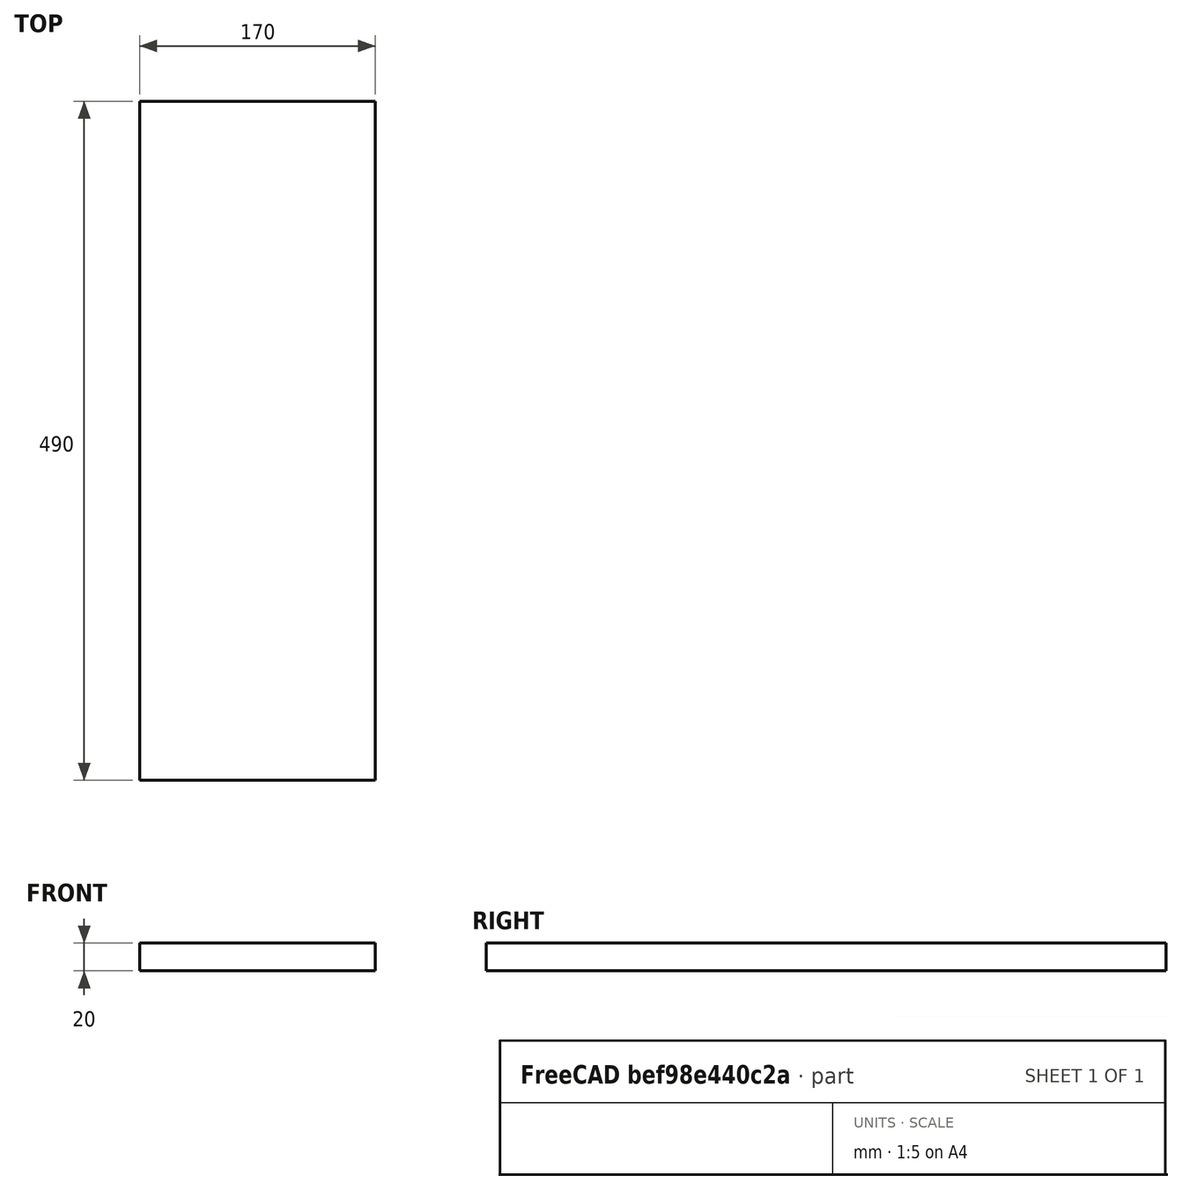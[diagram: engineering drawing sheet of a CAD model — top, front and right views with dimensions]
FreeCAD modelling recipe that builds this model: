
FCSTD DOCUMENT  (FreeCAD 0.18R16131 (Git))
Label: 700_ASM_Cabinet_Roof
License: All rights reserved
LicenseURL: http://en.wikipedia.org/wiki/All_rights_reserved
objects: Sketcher::SketchObject×1, PartDesign::Pad×1, PartDesign::Body×1, Spreadsheet::Sheet×1
note: 4 computed .brp shape members not serialized (recipe doc carries the construction recipe); baked Part::Feature solids carry a one-line shape summary decoded from their .brp

FEATURE [Sketcher::SketchObject] Sketch
  MapMode = 5
  Support = -> [XY_Plane]
  expr: Constraints[5] = xls.k_w
  sketch-geometry (5):
    g0: LineSegment StartX=0 StartY=490 StartZ=0 EndX=170 EndY=490 EndZ=0
    g1: LineSegment StartX=170 StartY=490 StartZ=0 EndX=170 EndY=0 EndZ=0
    g2: LineSegment StartX=170 StartY=0 StartZ=0 EndX=0 EndY=0 EndZ=0
    g3: LineSegment StartX=0 StartY=0 StartZ=0 EndX=0 EndY=245 EndZ=0
    g4: LineSegment StartX=0 StartY=245 StartZ=0 EndX=0 EndY=490 EndZ=0
  constraints (14):
    c: Coincident(g0,g1)
    c: Coincident(g1,g2)
    c: Horizontal(g0)
    c: Horizontal(g2)
    c: Vertical(g1)
    c: DistanceY(g1,g1) = 490
    c: DistanceX(g0,g0) = 170
    c: Coincident(g3,g2)
    c: Coincident(g4,g0)
    c: Equal(g3,g4)
    c: Vertical(g4)
    c: Vertical(g3)
    c: Coincident(g3,g4)
    c: Coincident(g2,g-1)
FEATURE [PartDesign::Pad] Pad
  Length = 20
  Length2 = 100
  Profile = -> Sketch
  Type = 0
  expr: Length = xls.k_t_0
FEATURE [PartDesign::Body] Body
  Group = -> [Sketch,Pad]
  Origin = -> Origin
  Tip = -> Pad
FEATURE [Spreadsheet::Sheet] Spreadsheet  label="xls"
  cells = B3=Marquee Top; B4=Orientation; D4=(0,0,1); B5=Thickness; C5=k_t_0; D5(k_t_0)=20; E5=mm; F5=10,13,16,19; B6=Width Y; C6=k_w; D6(k_w)=490; E6=mm; B7=Deapth X; C7=k_d; D7=100; E7=mm
